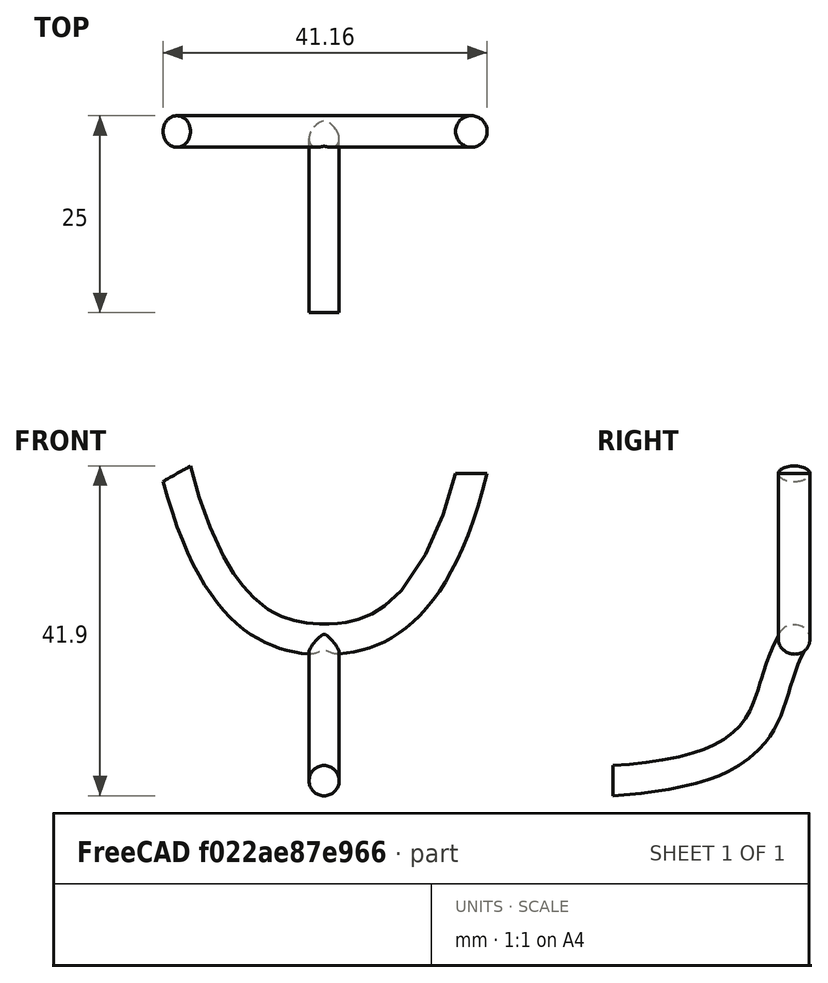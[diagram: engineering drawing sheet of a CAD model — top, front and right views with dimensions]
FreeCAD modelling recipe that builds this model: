
FCSTD DOCUMENT  (FreeCAD 0.19R24291 (Git))
Label: espeon
License: All rights reserved
LicenseURL: http://en.wikipedia.org/wiki/All_rights_reserved
objects: Sketcher::SketchObject×5, PartDesign::Body×2, PartDesign::AdditivePipe×2, Mesh::Feature×1, Part::Feature×1, Part::Refine×1, Part::Extrusion×1, Part::Cut×1
note: 15 computed .brp shape members not serialized (recipe doc carries the construction recipe); baked Part::Feature solids carry a one-line shape summary decoded from their .brp

FEATURE [Mesh::Feature] Espeon
FEATURE [Part::Feature] Espeon001
  shape: bbox 68.96 x 117 x 77.47 mm, 4058 faces, 0 solids (baked)
FEATURE [Part::Refine] Espeon001001
  Source = -> Espeon001
FEATURE [Sketcher::SketchObject] Sketch
  FullyConstrained = false
  MapMode = 5
  Placement = pos=(0,0,0) rot=(0.57735,0.57735,0.57735;2.0944rad)
  Support = -> [YZ_Plane]
  sketch-geometry (4):
    g0: LineSegment StartX=21.7257 StartY=42.5743 StartZ=0 EndX=85.4299 EndY=42.5743 EndZ=0
    g1: LineSegment StartX=85.4299 StartY=42.5743 StartZ=0 EndX=85.4299 EndY=31.0722 EndZ=0
    g2: LineSegment StartX=85.4299 StartY=31.0722 StartZ=0 EndX=21.7257 EndY=31.0722 EndZ=0
    g3: LineSegment StartX=21.7257 StartY=31.0722 StartZ=0 EndX=21.7257 EndY=42.5743 EndZ=0
  constraints (8):
    c: Coincident(g0,g1)
    c: Coincident(g1,g2)
    c: Coincident(g2,g3)
    c: Coincident(g3,g0)
    c: Horizontal(g0)
    c: Horizontal(g2)
    c: Vertical(g1)
    c: Vertical(g3)
FEATURE [PartDesign::Body] Body
  Group = -> [Sketch]
  Origin = -> Origin
FEATURE [Part::Extrusion] Extrude001
  Base = -> Sketch
  Dir = (1,-1e-16,1e-16)
  DirMode = 2
  FaceMakerClass = Part::FaceMakerBullseye
  LengthFwd = 40
  LengthRev = 0
  Solid = true
  Symmetric = true
FEATURE [Part::Cut] Cut
  Base = -> Espeon001001
  Refine = true
  Tool = -> Extrude001
FEATURE [Sketcher::SketchObject] Sketch001
  AttachmentOffset = pos=(0,0,-20) rot=(0,0,1;0rad)
  FullyConstrained = false
  MapMode = 5
  Placement = pos=(0,20,-4.4e-15) rot=(1,0,0;1.5708rad)
  Support = -> [XZ_Plane001]
  sketch-geometry (1):
    g0: Circle CenterX=0 CenterY=37 CenterZ=0 NormalX=0 NormalY=0 NormalZ=1 AngleXU=0 Radius=1.91953
  constraints (2):
    c: PointOnObject(g0,g-2)
    c: DistanceY(g-1,g0) = 37
FEATURE [Sketcher::SketchObject] Sketch002
  FullyConstrained = false
  MapMode = 5
  Placement = pos=(0,0,0) rot=(0.57735,0.57735,0.57735;2.0944rad)
  Support = -> [YZ_Plane001]
  sketch-geometry (7):
    g0-g3: Circle x4 (B-spline internal-alignment scaffolding for g4; pole/knot coordinates omitted)
    g4: BSplineCurve PolesCount=4 KnotsCount=2 Degree=3 IsPeriodic=0
    g5: GeomPoint X=20 Y=37 Z=0
    g6: GeomPoint X=43 Y=55 Z=0
  constraints (11):
    c: Weight(g0) = 1
    c: Equal(g0,g1)
    c: Equal(g0,g2)
    c: Equal(g0,g3)
    c: InternalAlignment(g0-g3 -> g4) x4
    c: InternalAlignment(g5,g4)
    c: InternalAlignment(g6,g4)
    c: DistanceX(g-1,g4) = 20
    c: DistanceY(g-1,g4) = 37
    c: DistanceX(g-1,g4) = 43
    c: DistanceY(g-1,g4) = 55
FEATURE [PartDesign::AdditivePipe] AdditivePipe
  AuxilleryCurvelinear = true
  AuxillerySpineTangent = false
  Binormal = (0,0,0)
  Mode = 0
  Placement = pos=(0,0,0) rot=(1,0,0;1.5708rad)
  Profile = -> Sketch001
  Refine = true
  Spine = -> Sketch002 [Edge1]
  SpineTangent = false
  Transformation = 0
  Transition = 0
FEATURE [Sketcher::SketchObject] Sketch003
  AttachmentOffset = pos=(0,0,-43) rot=(0,0,1;0rad)
  FullyConstrained = false
  MapMode = 5
  Placement = pos=(0,43,-9.5e-15) rot=(1,0,0;1.5708rad)
  Support = -> [XZ_Plane001]
  sketch-geometry (9):
    g0-g4: Circle x5 (B-spline internal-alignment scaffolding for g5; pole/knot coordinates omitted)
    g5: BSplineCurve PolesCount=5 KnotsCount=3 Degree=3 IsPeriodic=0
    g6: GeomPoint X=-18.7097 Y=76 Z=0
    g7: GeomPoint X=0 Y=54.9533 Z=0
    g8: GeomPoint X=18.7097 Y=76 Z=0
  constraints (11):
    c: Weight(g0) = 1
    c: Equal(g0, g1-g4) x4
    c: InternalAlignment(g0-g4 -> g5) x5
    c: InternalAlignment(g6,g5)
    c: InternalAlignment(g7,g5)
    c: InternalAlignment(g8,g5)
    c: PointOnObject(g2,g-2)
    c: Symmetric(g3,g1,g-2)
    c: Symmetric(g5,g5,g-2)
    c: DistanceY(g-1,g7) = 54.9533
    c: DistanceY(g-1,g5) = 76
FEATURE [Sketcher::SketchObject] Sketch004
  AttachmentOffset = pos=(0,0,76) rot=(0,0,1;0rad)
  ExternalGeometry = -> [Sketch003]
  FullyConstrained = true
  MapMode = 5
  Placement = pos=(0,0,76) rot=(0,0,1;0rad)
  Support = -> [XY_Plane001]
  sketch-geometry (1):
    g0: Circle CenterX=18.7097 CenterY=43 CenterZ=0 NormalX=0 NormalY=0 NormalZ=1 AngleXU=0 Radius=2
  constraints (2):
    c: Coincident(g0,g-3)
    c: Radius(g0) = 2
FEATURE [PartDesign::AdditivePipe] AdditivePipe001
  AuxilleryCurvelinear = true
  AuxillerySpineTangent = false
  BaseFeature = -> AdditivePipe
  Binormal = (0,0,0)
  Mode = 0
  Placement = pos=(0,0,0) rot=(1,0,0;1.5708rad)
  Profile = -> Sketch004
  Refine = true
  Spine = -> Sketch003 [Edge1]
  SpineTangent = false
  Transformation = 0
  Transition = 2
FEATURE [PartDesign::Body] Body001
  Group = -> [Sketch001,Sketch002,AdditivePipe,Sketch003,Sketch004,AdditivePipe001]
  Origin = -> Origin001
  Tip = -> AdditivePipe001
